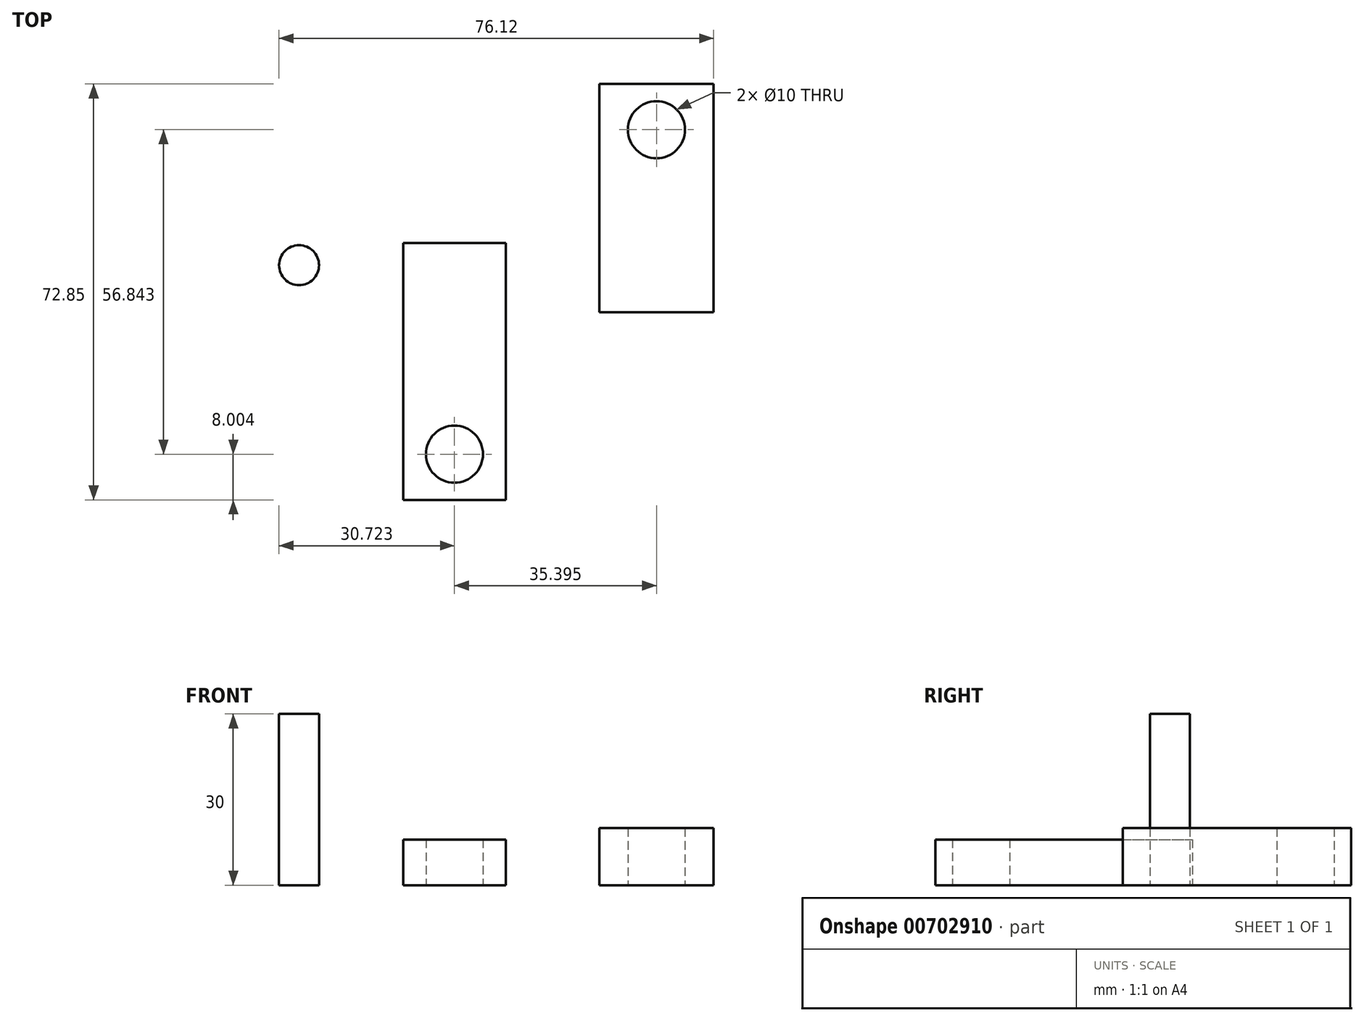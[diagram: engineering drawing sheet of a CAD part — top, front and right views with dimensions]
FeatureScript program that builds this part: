
annotation { "Feature Type Name" : "Feature", "Feature Type Description" : "" }
export const myFeature = defineFeature(function(context is Context, id is Id, definition is map)
    precondition{}
    {
        {
            var Q0;
            Q0=qCreatedBy(makeId("Top.planeOp"),FACE);
            var sketch = newSketch(context, id + "F0", { "sketchPlane" : qUnion([Q0])});
            skLineSegment(sketch, "E0.bottom", {"start": v(-2, 3) * mm, "end": v(18, 3) * mm});
            skLineSegment(sketch, "E0.top", {"start": v(-2, 43) * mm, "end": v(18, 43) * mm});
            skLineSegment(sketch, "E0.left", {"start": v(-2, 3) * mm, "end": v(-2, 43) * mm});
            skLineSegment(sketch, "E0.right", {"start": v(18, 3) * mm, "end": v(18, 43) * mm});
            skCircle(sketch, "E1", {"center": v(8, 35) * mm, "radius": 5 * mm});
            skSolve(sketch);
        }
        {
            var Q0;
            Q0=makeQuery(id+"F0.imprint","IMPRINT",FACE,{"disambiguationData":[TD([[makeQuery(id+"F0.imprint","IMPRINT",EDGE,{"derivedFrom":sQuery(id+"F0.wireOp",EDGE,"E0.bottom")}),1.0]])]});
            extrude(context, id + "F1", {"entities" : qUnion([Q0]), "depth" : 10 * mm, "offsetDistance" : 25 * mm});
        }
        {
            var Q0;
            Q0=qCreatedBy(makeId("Top.planeOp"),FACE);
            var sketch = newSketch(context, id + "F2", { "sketchPlane" : qUnion([Q0])});
            skCircle(sketch, "E2", {"center": v(-54.62, 11.27) * mm, "radius": 3.5 * mm});
            skSolve(sketch);
        }
        {
            var Q0;
            Q0=makeQuery(id+"F2.imprint","IMPRINT",FACE,{"disambiguationData":[TD([[makeQuery(id+"F2.imprint","IMPRINT",EDGE,{"derivedFrom":sQuery(id+"F2.wireOp",EDGE,"E2")}),1.0]])]});
            extrude(context, id + "F3", {"entities" : qUnion([Q0]), "depth" : 30 * mm, "offsetDistance" : 25 * mm});
        }
        {
            var Q0;
            Q0=qCreatedBy(makeId("Top.planeOp"),FACE);
            var sketch = newSketch(context, id + "F4", { "sketchPlane" : qUnion([Q0])});
            skLineSegment(sketch, "E3.bottom", {"start": v(-36.4, -29.84) * mm, "end": v(-18.4, -29.84) * mm});
            skLineSegment(sketch, "E3.top", {"start": v(-36.4, 15.16) * mm, "end": v(-18.4, 15.16) * mm});
            skLineSegment(sketch, "E3.left", {"start": v(-36.4, -29.84) * mm, "end": v(-36.4, 15.16) * mm});
            skLineSegment(sketch, "E3.right", {"start": v(-18.4, -29.84) * mm, "end": v(-18.4, 15.16) * mm});
            skCircle(sketch, "E4", {"center": v(-27.4, -21.84) * mm, "radius": 5 * mm});
            skSolve(sketch);
        }
        {
            var Q0;
            Q0=makeQuery(id+"F4.imprint","IMPRINT",FACE,{"disambiguationData":[TD([[makeQuery(id+"F4.imprint","IMPRINT",EDGE,{"derivedFrom":sQuery(id+"F4.wireOp",EDGE,"E3.bottom")}),1.0]])]});
            extrude(context, id + "F5", {"entities" : qUnion([Q0]), "depth" : 8 * mm, "offsetDistance" : 25 * mm});
        }
    });
